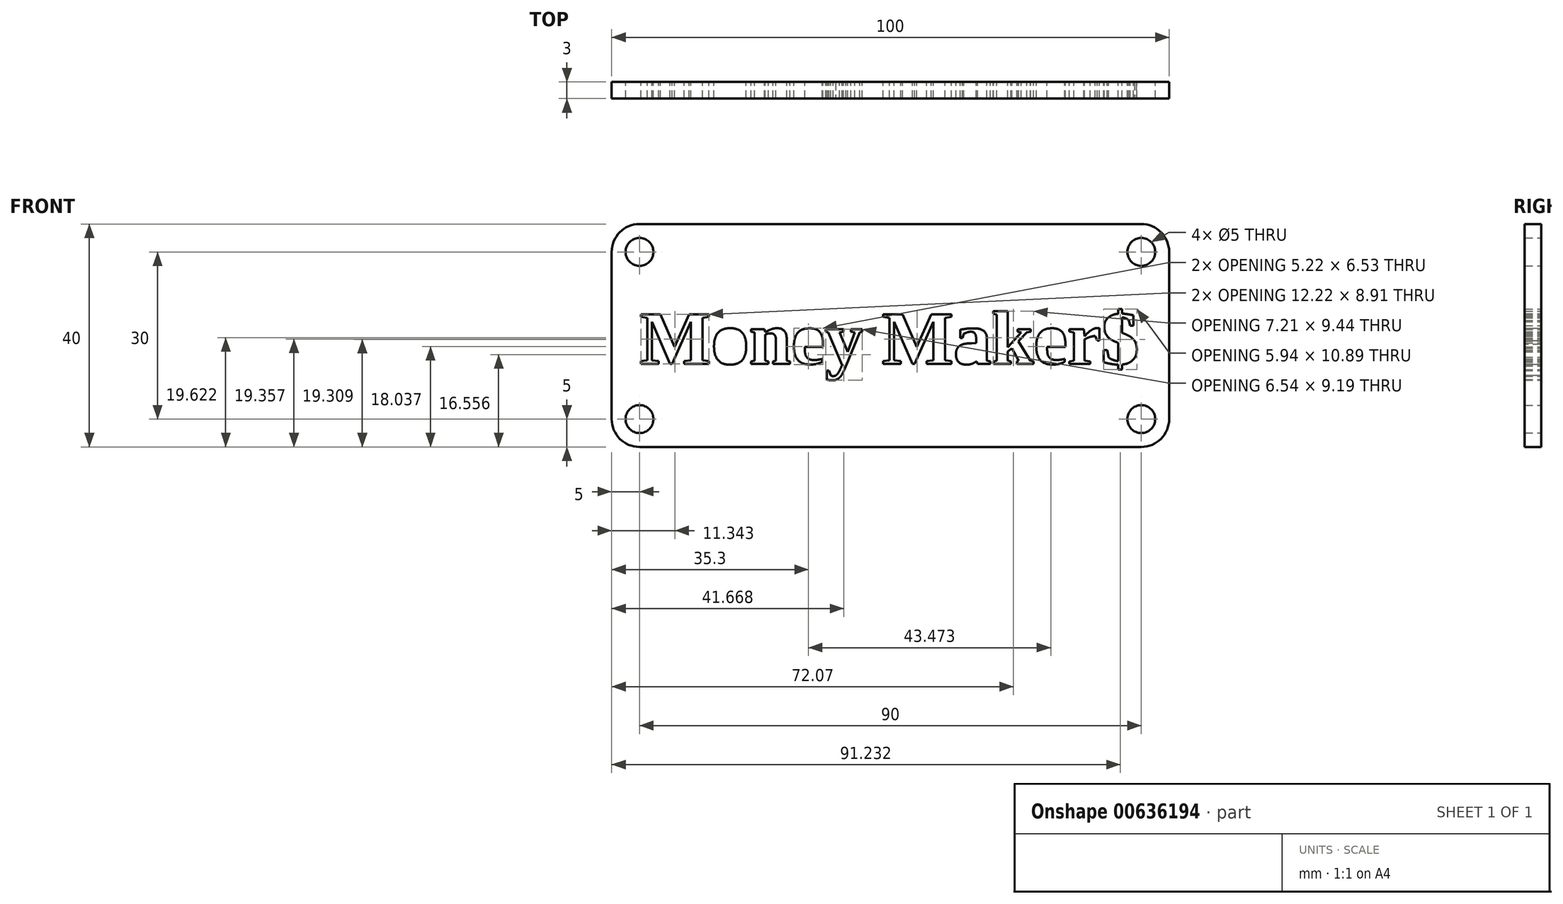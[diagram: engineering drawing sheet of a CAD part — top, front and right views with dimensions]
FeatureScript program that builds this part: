
annotation { "Feature Type Name" : "Feature", "Feature Type Description" : "" }
export const myFeature = defineFeature(function(context is Context, id is Id, definition is map)
    precondition{}
    {
        {
            var Q0;
            Q0=qCreatedBy(makeId("Front.planeOp"),FACE);
            var sketch = newSketch(context, id + "F0", { "sketchPlane" : qUnion([Q0])});
            skLineSegment(sketch, "E0.bottom", {"start": v(5, 0) * mm, "end": v(95, 0) * mm});
            skLineSegment(sketch, "E0.top", {"start": v(5, 40) * mm, "end": v(95, 40) * mm});
            skLineSegment(sketch, "E0.left", {"start": v(0, 5) * mm, "end": v(0, 35) * mm});
            skLineSegment(sketch, "E0.right", {"start": v(100, 5) * mm, "end": v(100, 35) * mm});
            skText(sketch, "E1", { "text": "Money Maker$\n", "fontName": "Tinos-Bold.ttf"});
            skPoint(sketch, "E2.visualSharp", {"position": v(0, 40) * mm});
            skArc(sketch, "E2.filletArc", {"start": v(5, 40) * mm, "mid": v(1.46, 38.54) * mm, "end": v(0, 35) * mm});
            skPoint(sketch, "E3.visualSharp", {"position": v(100, 40) * mm});
            skArc(sketch, "E3.filletArc", {"start": v(100, 35) * mm, "mid": v(98.54, 38.54) * mm, "end": v(95, 40) * mm});
            skPoint(sketch, "E4.visualSharp", {"position": v(100, 0) * mm});
            skArc(sketch, "E4.filletArc", {"start": v(95, 0) * mm, "mid": v(98.54, 1.46) * mm, "end": v(100, 5) * mm});
            skPoint(sketch, "E5.visualSharp", {"position": v(0, 0) * mm});
            skArc(sketch, "E5.filletArc", {"start": v(0, 5) * mm, "mid": v(1.46, 1.46) * mm, "end": v(5, 0) * mm});
            skCircle(sketch, "E6", {"center": v(5, 35) * mm, "radius": 2.5 * mm});
            skCircle(sketch, "E7", {"center": v(95, 35) * mm, "radius": 2.5 * mm});
            skCircle(sketch, "E8", {"center": v(5, 5) * mm, "radius": 2.5 * mm});
            skCircle(sketch, "E9", {"center": v(95, 5) * mm, "radius": 2.5 * mm});
            const initialGuessF0  = {"E1": [0.005, 0.0149, 1, 0, 0.0098]};
            skSetInitialGuess(sketch, initialGuessF0);
            skSolve(sketch);
        }
        {
            var Q0;
            Q0=makeQuery(id+"F0.imprint","IMPRINT",FACE,{"disambiguationData":[TD([[makeQuery(id+"F0.imprint","IMPRINT",EDGE,{"derivedFrom":sQuery(id+"F0.wireOp",EDGE,"E0.bottom")}),1.0]])]});
            extrude(context, id + "F1", {"entities" : qUnion([Q0]), "depth" : 3 * mm, "offsetDistance" : 25 * mm});
        }
    });
